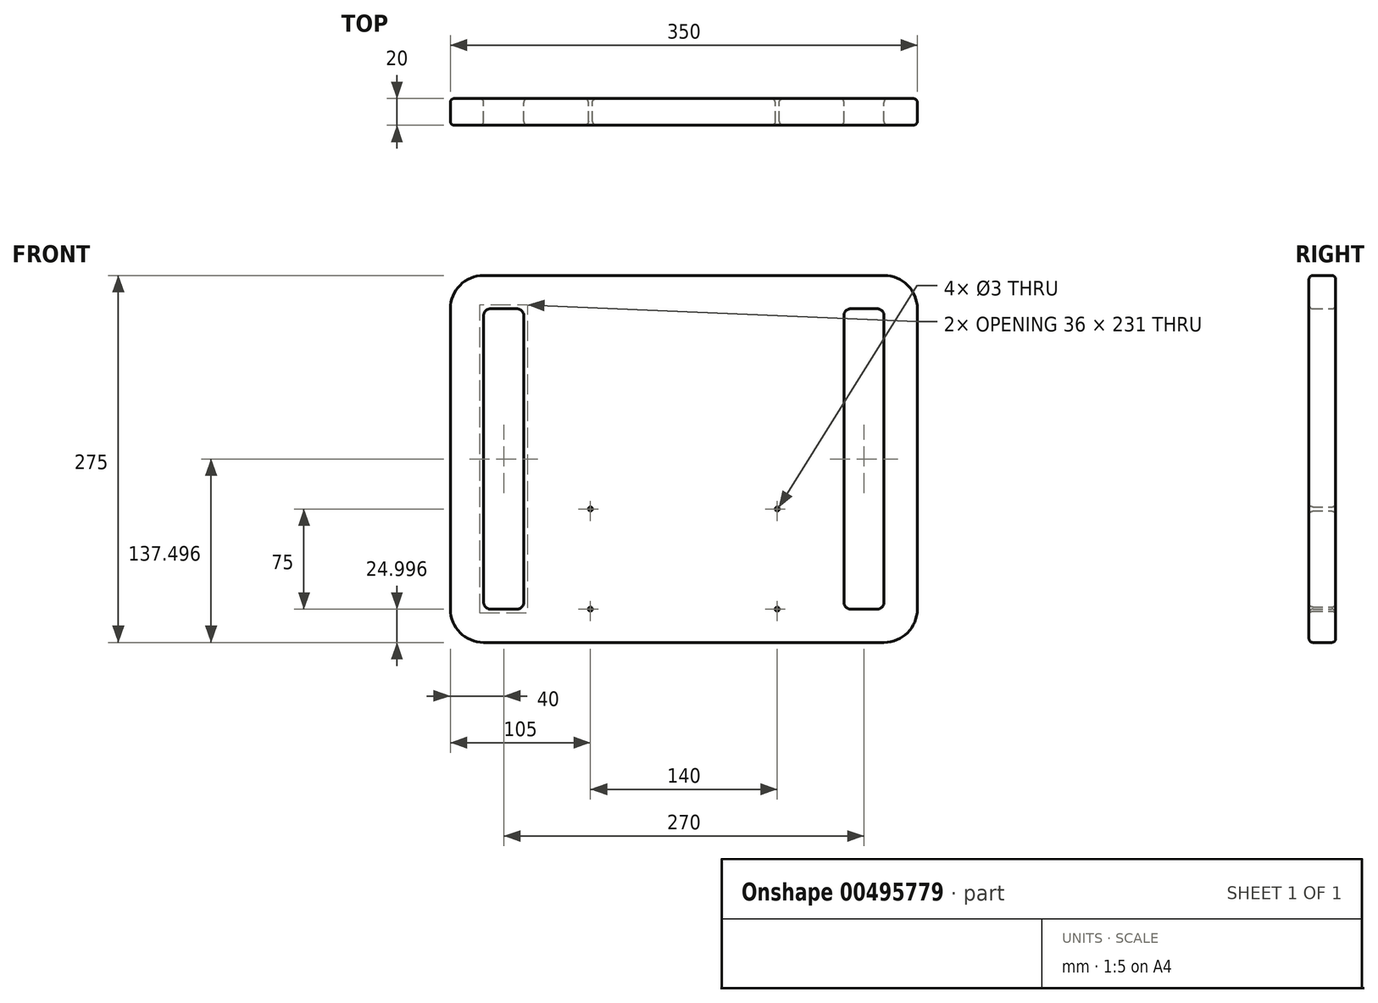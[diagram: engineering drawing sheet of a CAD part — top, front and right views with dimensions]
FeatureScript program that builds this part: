
annotation { "Feature Type Name" : "Feature", "Feature Type Description" : "" }
export const myFeature = defineFeature(function(context is Context, id is Id, definition is map)
    precondition{}
    {
        {
            var Q0;
            Q0=qCreatedBy(makeId("Front.planeOp"),FACE);
            var sketch = newSketch(context, id + "F0", { "sketchPlane" : qUnion([Q0])});
            skPoint(sketch, "E0", {"position": v(0, -0.73) * mm});
            skLineSegment(sketch, "E1", {"start": v(0, 24.04) * mm, "end": v(0, -0.73) * mm});
            skLineSegment(sketch, "E2", {"start": v(0, 174.27) * mm, "end": v(-150, 174.27) * mm});
            skLineSegment(sketch, "E3", {"start": v(-175, 149.27) * mm, "end": v(-175, 24.27) * mm});
            skLineSegment(sketch, "E4", {"start": v(-150, -100.73) * mm, "end": v(0, -100.73) * mm});
            skLineSegment(sketch, "E5", {"start": v(-175, 24.27) * mm, "end": v(-175, -75.73) * mm});
            skPoint(sketch, "E6.visualSharp", {"position": v(-175, 174.27) * mm});
            skArc(sketch, "E6.filletArc", {"start": v(-150, 174.27) * mm, "mid": v(-167.68, 166.94) * mm, "end": v(-175, 149.27) * mm});
            skPoint(sketch, "E7.visualSharp", {"position": v(-175, -100.73) * mm});
            skArc(sketch, "E7.filletArc", {"start": v(-175, -75.73) * mm, "mid": v(-167.68, -93.41) * mm, "end": v(-150, -100.73) * mm});
            skCircle(sketch, "E8", {"center": v(-70, -0.73) * mm, "radius": 1.5 * mm});
            skCircle(sketch, "E9", {"center": v(-70, -75.73) * mm, "radius": 1.5 * mm});
            skLineSegment(sketch, "E10.MirrorCS", {"start": v(0, 174.27) * mm, "end": v(150, 174.27) * mm});
            skArc(sketch, "E11.MirrorCS", {"start": v(150, 174.27) * mm, "mid": v(167.68, 166.94) * mm, "end": v(175, 149.27) * mm});
            skLineSegment(sketch, "E12.MirrorCS", {"start": v(175, 149.27) * mm, "end": v(175, 24.27) * mm});
            skArc(sketch, "E13.MirrorCS", {"start": v(175, -75.73) * mm, "mid": v(167.68, -93.41) * mm, "end": v(150, -100.73) * mm});
            skLineSegment(sketch, "E14.MirrorCS", {"start": v(150, -100.73) * mm, "end": v(0, -100.73) * mm});
            skLineSegment(sketch, "E15.MirrorCS", {"start": v(175, 24.27) * mm, "end": v(175, -75.73) * mm});
            skCircle(sketch, "E16.MirrorC", {"center": v(70, -0.73) * mm, "radius": 1.5 * mm});
            skCircle(sketch, "E17.MirrorC", {"center": v(70, -75.73) * mm, "radius": 1.5 * mm});
            skLineSegment(sketch, "E18", {"start": v(0, -0.73) * mm, "end": v(0, -82.47) * mm});
            skLineSegment(sketch, "E19", {"start": v(0, -82.47) * mm, "end": v(0, 86.66) * mm});
            skLineSegment(sketch, "E20", {"start": v(-70, -0.73) * mm, "end": v(0, -0.73) * mm});
            skLineSegment(sketch, "E21", {"start": v(0, -0.73) * mm, "end": v(70, -0.73) * mm});
            skLineSegment(sketch, "E22", {"start": v(70, -75.73) * mm, "end": v(0, -75.73) * mm});
            skLineSegment(sketch, "E23", {"start": v(0, -75.73) * mm, "end": v(-70, -75.73) * mm});
            skLineSegment(sketch, "E24", {"start": v(-70, -75.73) * mm, "end": v(-70, -100.73) * mm});
            skLineSegment(sketch, "E25.bottom", {"start": v(-145, 149.27) * mm, "end": v(-125, 149.27) * mm});
            skLineSegment(sketch, "E25.top", {"start": v(-145, -75.73) * mm, "end": v(-125, -75.73) * mm});
            skLineSegment(sketch, "E25.left", {"start": v(-150, 144.27) * mm, "end": v(-150, -70.73) * mm});
            skLineSegment(sketch, "E25.right", {"start": v(-120, 144.27) * mm, "end": v(-120, -70.73) * mm});
            skLineSegment(sketch, "E26.bottom", {"start": v(145, 149.27) * mm, "end": v(125, 149.27) * mm});
            skLineSegment(sketch, "E26.top", {"start": v(145, -75.73) * mm, "end": v(125, -75.73) * mm});
            skLineSegment(sketch, "E26.left", {"start": v(150, 144.27) * mm, "end": v(150, -70.73) * mm});
            skLineSegment(sketch, "E26.right", {"start": v(120, 144.27) * mm, "end": v(120, -70.73) * mm});
            skArc(sketch, "E27.filletArc", {"start": v(-145, 149.27) * mm, "mid": v(-148.54, 147.8) * mm, "end": v(-150, 144.27) * mm});
            skPoint(sketch, "E28.visualSharp", {"position": v(-120, 149.27) * mm});
            skArc(sketch, "E28.filletArc", {"start": v(-120, 144.27) * mm, "mid": v(-121.46, 147.8) * mm, "end": v(-125, 149.27) * mm});
            skPoint(sketch, "E29.visualSharp", {"position": v(-120, -75.73) * mm});
            skArc(sketch, "E29.filletArc", {"start": v(-125, -75.73) * mm, "mid": v(-121.46, -74.27) * mm, "end": v(-120, -70.73) * mm});
            skArc(sketch, "E30.filletArc", {"start": v(-150, -70.73) * mm, "mid": v(-148.54, -74.27) * mm, "end": v(-145, -75.73) * mm});
            skArc(sketch, "E31.filletArc", {"start": v(150, 144.27) * mm, "mid": v(148.54, 147.8) * mm, "end": v(145, 149.27) * mm});
            skArc(sketch, "E32.filletArc", {"start": v(145, -75.73) * mm, "mid": v(148.54, -74.27) * mm, "end": v(150, -70.73) * mm});
            skPoint(sketch, "E33.visualSharp", {"position": v(120, -75.73) * mm});
            skArc(sketch, "E33.filletArc", {"start": v(120, -70.73) * mm, "mid": v(121.46, -74.27) * mm, "end": v(125, -75.73) * mm});
            skPoint(sketch, "E34.visualSharp", {"position": v(120, 149.27) * mm});
            skArc(sketch, "E34.filletArc", {"start": v(125, 149.27) * mm, "mid": v(121.46, 147.8) * mm, "end": v(120, 144.27) * mm});
            skSolve(sketch);
        }
        {
            var Q0;
            Q0=makeQuery(id+"F0.imprint","IMPRINT",FACE,{"disambiguationData":[TD([[makeQuery(id+"F0.imprint","IMPRINT",EDGE,{"derivedFrom":sQuery(id+"F0.wireOp",EDGE,"E2")}),1.0]])]});
            extrude(context, id + "F1", {"entities" : qUnion([Q0]), "endBound" : BoundingType.SYMMETRIC, "depth" : 20 * mm});
        }
        {
            var Q0;
            Q0=makeQuery(id+"F1.opExtrude","CAP_FACE",FACE,{"disambiguationData":[OSD([sQuery(id+"F0.wireOp",EDGE,"E2"),sQuery(id+"F0.wireOp",EDGE,"E3"),sQuery(id+"F0.wireOp",EDGE,"E4"),sQuery(id+"F0.wireOp",EDGE,"E5"),sQuery(id+"F0.wireOp",EDGE,"E6.filletArc"),sQuery(id+"F0.wireOp",EDGE,"E7.filletArc"),sQuery(id+"F0.wireOp",EDGE,"E8"),sQuery(id+"F0.wireOp",EDGE,"E9"),sQuery(id+"F0.wireOp",EDGE,"E10.MirrorCS"),sQuery(id+"F0.wireOp",EDGE,"E11.MirrorCS"),sQuery(id+"F0.wireOp",EDGE,"E12.MirrorCS"),sQuery(id+"F0.wireOp",EDGE,"E13.MirrorCS"),sQuery(id+"F0.wireOp",EDGE,"E14.MirrorCS"),sQuery(id+"F0.wireOp",EDGE,"E15.MirrorCS"),sQuery(id+"F0.wireOp",EDGE,"E16.MirrorC"),sQuery(id+"F0.wireOp",EDGE,"E17.MirrorC")])],"isStart":true});
            var Q1;
            Q1=makeQuery(id+"F1.opExtrude","CAP_FACE",FACE,{"disambiguationData":[OSD([sQuery(id+"F0.wireOp",EDGE,"E2"),sQuery(id+"F0.wireOp",EDGE,"E3"),sQuery(id+"F0.wireOp",EDGE,"E4"),sQuery(id+"F0.wireOp",EDGE,"E5"),sQuery(id+"F0.wireOp",EDGE,"E6.filletArc"),sQuery(id+"F0.wireOp",EDGE,"E7.filletArc"),sQuery(id+"F0.wireOp",EDGE,"E8"),sQuery(id+"F0.wireOp",EDGE,"E9"),sQuery(id+"F0.wireOp",EDGE,"E10.MirrorCS"),sQuery(id+"F0.wireOp",EDGE,"E11.MirrorCS"),sQuery(id+"F0.wireOp",EDGE,"E12.MirrorCS"),sQuery(id+"F0.wireOp",EDGE,"E13.MirrorCS"),sQuery(id+"F0.wireOp",EDGE,"E14.MirrorCS"),sQuery(id+"F0.wireOp",EDGE,"E15.MirrorCS"),sQuery(id+"F0.wireOp",EDGE,"E16.MirrorC"),sQuery(id+"F0.wireOp",EDGE,"E17.MirrorC")])],"isStart":false});
            fillet(context, id + "F2", {"entities" : qUnion([Q0, Q1]), "radius" : 3 * mm, "tangentPropagation" : true, "allowEdgeOverflow" : false});
        }
    });
